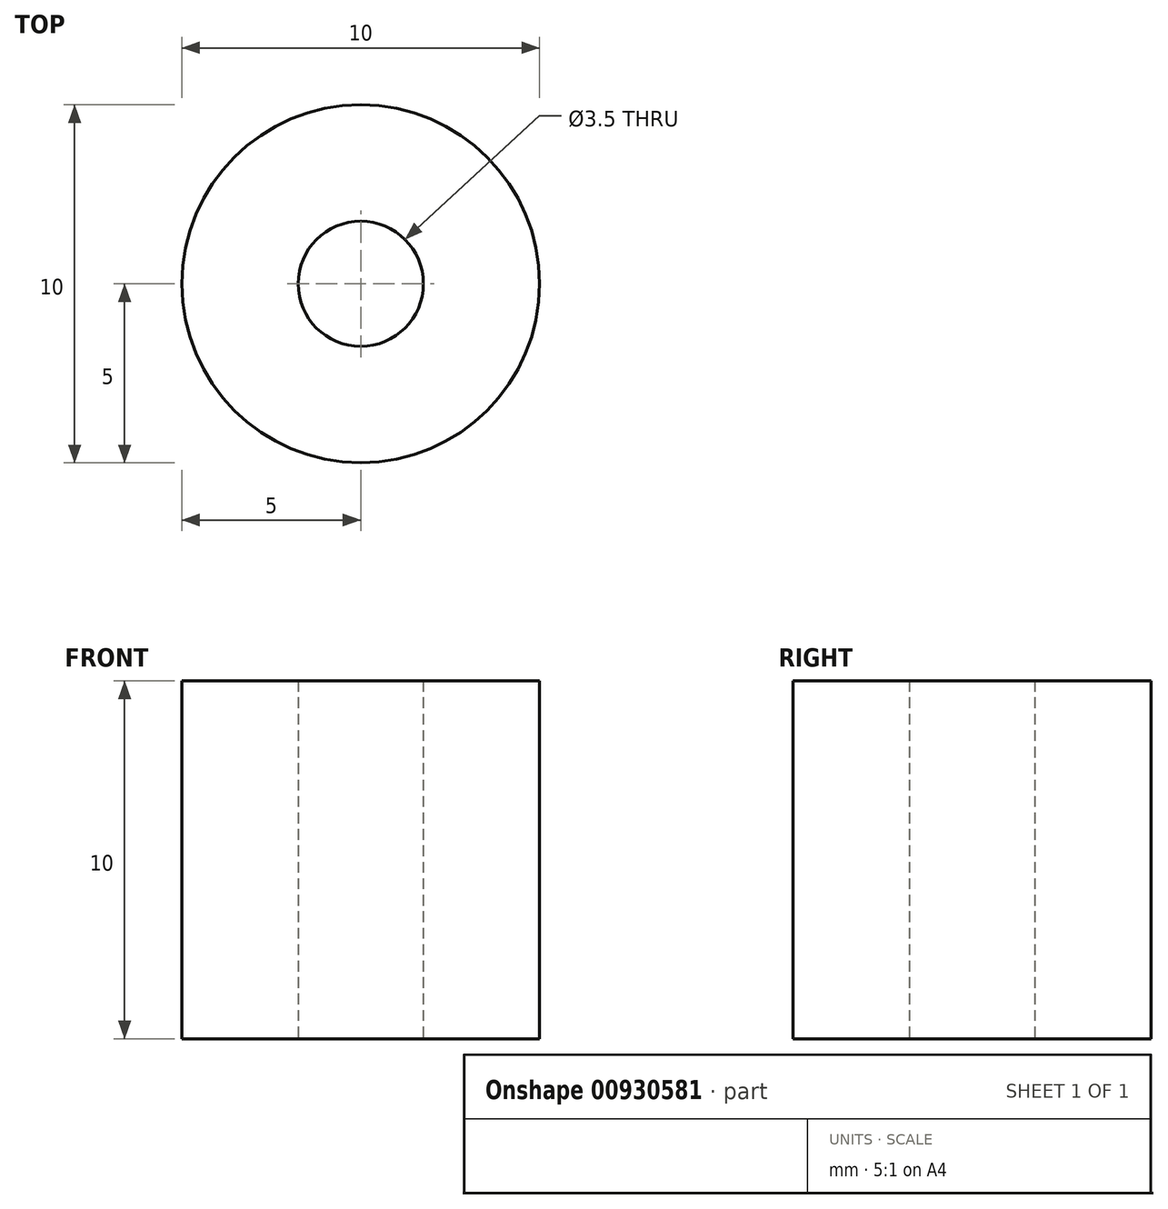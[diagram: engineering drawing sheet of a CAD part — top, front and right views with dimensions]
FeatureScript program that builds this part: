
annotation { "Feature Type Name" : "Feature", "Feature Type Description" : "" }
export const myFeature = defineFeature(function(context is Context, id is Id, definition is map)
    precondition{}
    {
        {
            var Q0;
            Q0=qCreatedBy(makeId("Top.planeOp"),FACE);
            var sketch = newSketch(context, id + "F0", { "sketchPlane" : qUnion([Q0])});
            skCircle(sketch, "E0", {"center": v(0, 0) * mm, "radius": 5 * mm});
            skCircle(sketch, "E1", {"center": v(0, 0) * mm, "radius": 1.75 * mm});
            skSolve(sketch);
        }
        {
            var Q0;
            Q0=qSketchRegion(id+"F0",true);
            extrude(context, id + "F1", {"entities" : qUnion([Q0]), "depth" : 10 * mm});
        }
    });
